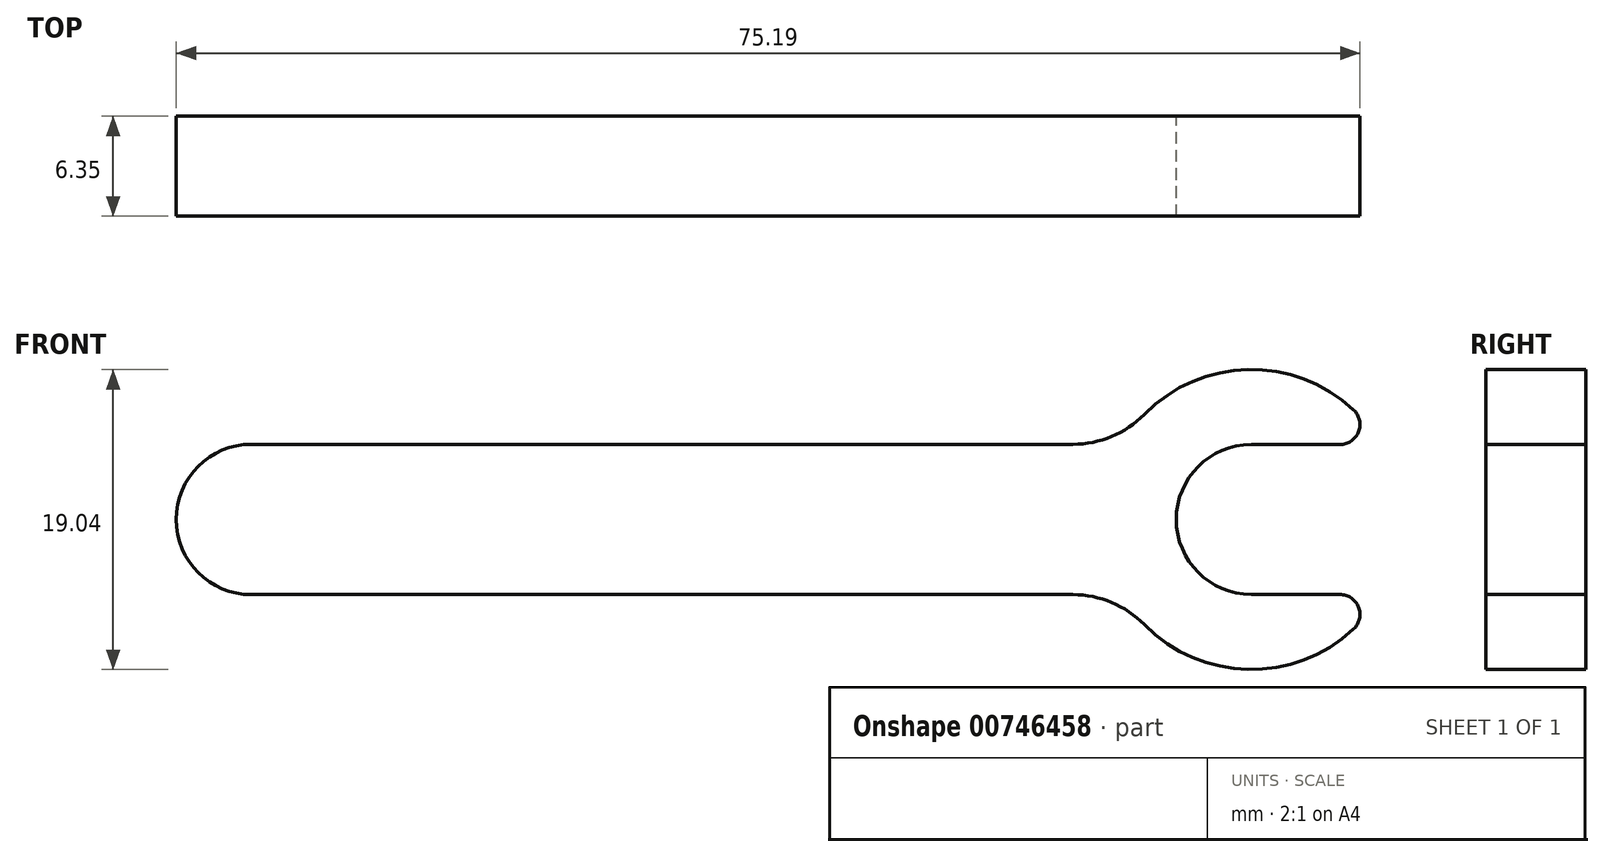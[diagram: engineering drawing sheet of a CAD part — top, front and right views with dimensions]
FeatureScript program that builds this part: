
annotation { "Feature Type Name" : "Feature", "Feature Type Description" : "" }
export const myFeature = defineFeature(function(context is Context, id is Id, definition is map)
    precondition{}
    {
        {
            var Q0;
            Q0=qCreatedBy(makeId("Front.planeOp"),FACE);
            var sketch = newSketch(context, id + "F0", { "sketchPlane" : qUnion([Q0])});
            skArc(sketch, "E0", {"start": v(0, 4.78) * mm, "mid": v(-4.78, 0) * mm, "end": v(0, -4.78) * mm});
            skArc(sketch, "E1", {"start": v(63.5, 4.76) * mm, "mid": v(58.74, 0) * mm, "end": v(63.5, -4.76) * mm});
            skArc(sketch, "E2", {"start": v(70, 6.96) * mm, "mid": v(63.3, 9.52) * mm, "end": v(56.7, 6.68) * mm});
            skArc(sketch, "E3.filletArc", {"start": v(52.18, 4.78) * mm, "mid": v(54.63, 5.27) * mm, "end": v(56.7, 6.68) * mm});
            skLineSegment(sketch, "E4", {"start": v(0, -4.78) * mm, "end": v(52.18, -4.78) * mm});
            skLineSegment(sketch, "E5", {"start": v(0, 4.78) * mm, "end": v(52.18, 4.78) * mm});
            skArc(sketch, "E6.MirrorCS", {"start": v(52.18, -4.78) * mm, "mid": v(54.63, -5.27) * mm, "end": v(56.7, -6.68) * mm});
            skLineSegment(sketch, "E7", {"start": v(63.5, 4.76) * mm, "end": v(69.14, 4.76) * mm});
            skArc(sketch, "E8.filletArc", {"start": v(69.14, 4.76) * mm, "mid": v(70.32, 5.57) * mm, "end": v(70, 6.96) * mm});
            skLineSegment(sketch, "E9.MirrorCS", {"start": v(63.5, -4.76) * mm, "end": v(69.14, -4.76) * mm});
            skArc(sketch, "E10.MirrorCS", {"start": v(69.14, -4.76) * mm, "mid": v(70.32, -5.57) * mm, "end": v(70, -6.96) * mm});
            skArc(sketch, "E11.MirrorCS", {"start": v(70, -6.96) * mm, "mid": v(63.3, -9.52) * mm, "end": v(56.7, -6.68) * mm});
            skLineSegment(sketch, "E12", {"start": v(0, 0) * mm, "end": v(63.5, 0) * mm});
            skSolve(sketch);
        }
        {
            var Q0;
            Q0=makeQuery(id+"F0.imprint","IMPRINT",FACE,{"disambiguationData":[TD([[makeQuery(id+"F0.imprint","IMPRINT",EDGE,{"derivedFrom":sQuery(id+"F0.wireOp",EDGE,"E0")}),1.0]])]});
            extrude(context, id + "F1", {"entities" : qUnion([Q0]), "depth" : 6.35 * mm, "offsetDistance" : 25.4 * mm});
        }
    });
